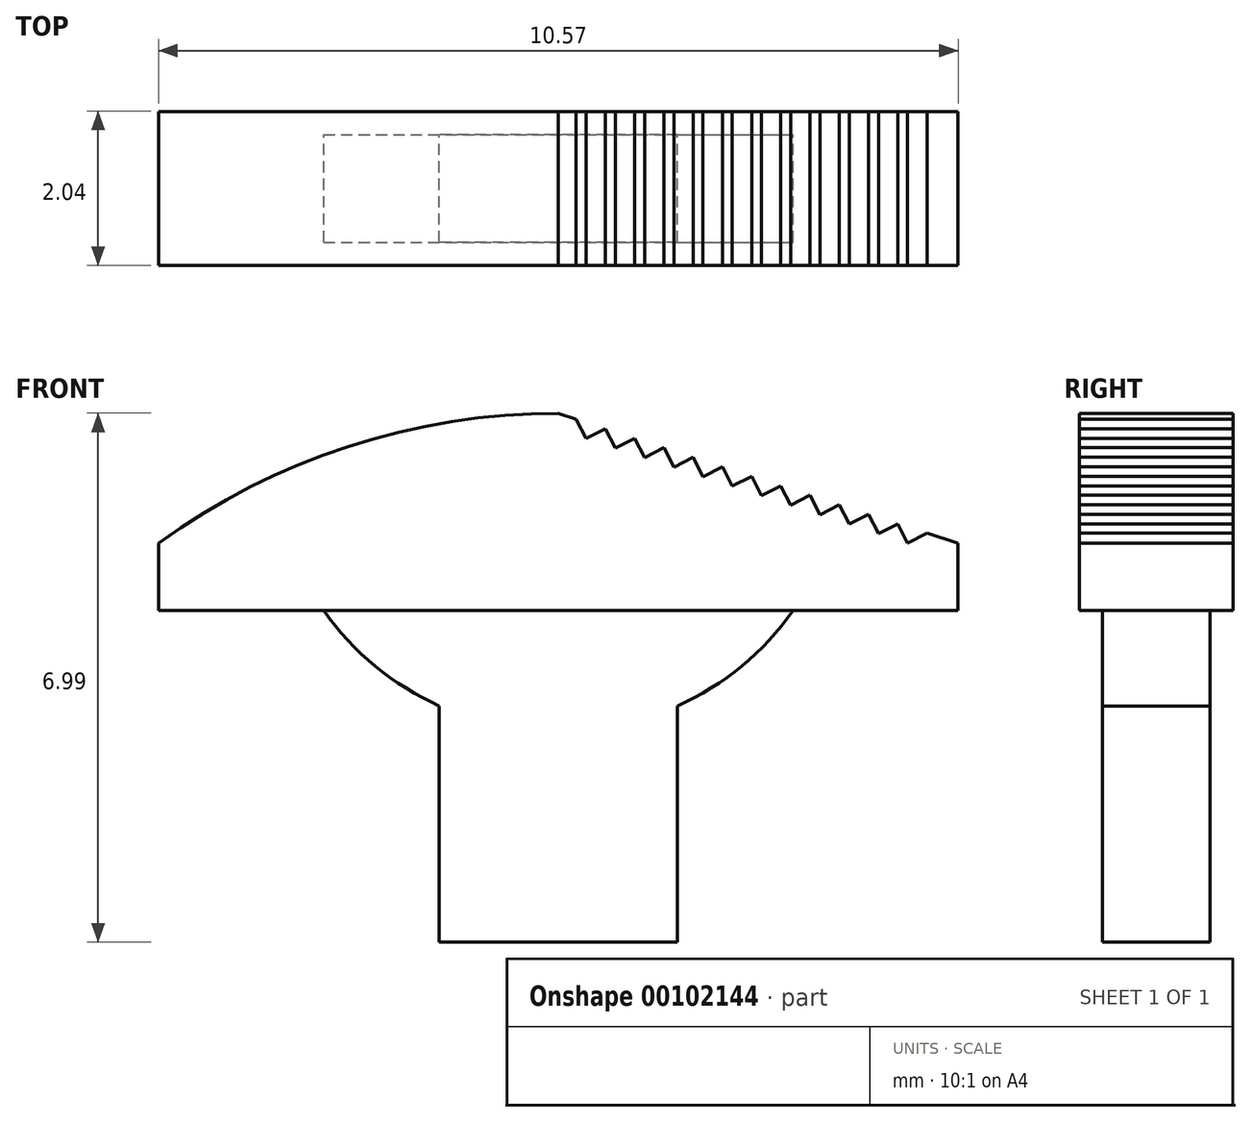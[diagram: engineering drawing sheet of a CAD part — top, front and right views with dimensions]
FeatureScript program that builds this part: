
annotation { "Feature Type Name" : "Feature", "Feature Type Description" : "" }
export const myFeature = defineFeature(function(context is Context, id is Id, definition is map)
    precondition{}
    {
        {
            var Q0;
            Q0=qCreatedBy(makeId("Front.planeOp"),FACE);
            var sketch = newSketch(context, id + "F0", { "sketchPlane" : qUnion([Q0])});
            skLineSegment(sketch, "E0", {"start": v(0, 0) * mm, "end": v(-3.15, 0) * mm});
            skLineSegment(sketch, "E1", {"start": v(-3.15, 0) * mm, "end": v(-3.15, 3.12) * mm});
            skLineSegment(sketch, "E2", {"start": v(3.7, 4.38) * mm, "end": v(1.53, 4.38) * mm});
            skLineSegment(sketch, "E3", {"start": v(-6.86, 4.38) * mm, "end": v(-6.86, 5.27) * mm});
            skLineSegment(sketch, "E4", {"start": v(3.7, 5.27) * mm, "end": v(3.7, 4.38) * mm});
            skArc(sketch, "E5", {"start": v(-4.68, 4.38) * mm, "mid": v(-4, 3.65) * mm, "end": v(-3.15, 3.12) * mm});
            skLineSegment(sketch, "E6", {"start": v(0, 0) * mm, "end": v(0, 3.12) * mm});
            skPoint(sketch, "E7", {"position": v(-1.57, 0) * mm});
            skLineSegment(sketch, "E8.trimOffspring", {"start": v(-4.68, 4.38) * mm, "end": v(-6.86, 4.38) * mm});
            skArc(sketch, "E9.trimOffspring", {"start": v(0, 3.12) * mm, "mid": v(0.85, 3.65) * mm, "end": v(1.53, 4.38) * mm});
            skArc(sketch, "E10", {"start": v(-1.57, 6.99) * mm, "mid": v(-4.35, 6.55) * mm, "end": v(-6.86, 5.27) * mm});
            skLineSegment(sketch, "E11", {"start": v(-1.57, 6.99) * mm, "end": v(3.7, 5.27) * mm});
            skLineSegment(sketch, "E12", {"start": v(-4.68, 4.38) * mm, "end": v(1.53, 4.38) * mm});
            skSolve(sketch);
        }
        {
            var Q0;
            Q0=makeQuery(id+"F0.imprint","IMPRINT",FACE,{"disambiguationData":[TD([[makeQuery(id+"F0.imprint","IMPRINT",EDGE,{"derivedFrom":sQuery(id+"F0.wireOp",EDGE,"E2")}),-1.0]])]});
            extrude(context, id + "F1", {"entities" : qUnion([Q0]), "depth" : 1.02 * mm, "hasSecondDirection" : true, "secondDirectionOppositeDirection" : true, "secondDirectionDepth" : 1.02 * mm});
        }
        {
            var Q0;
            Q0=makeQuery(id+"F0.imprint","IMPRINT",FACE,{"disambiguationData":[TD([[makeQuery(id+"F0.imprint","IMPRINT",EDGE,{"derivedFrom":sQuery(id+"F0.wireOp",EDGE,"E0")}),-1.0]])]});
            extrude(context, id + "F2", {"entities" : qUnion([Q0]), "operationType" : NewBodyOperationType.ADD, "depth" : 0.71 * mm, "hasSecondDirection" : true, "secondDirectionOppositeDirection" : true, "secondDirectionDepth" : 0.71 * mm});
        }
        {
            var Q0;
            Q0=makeQuery(id+"F1.opExtrude","CAP_FACE",FACE,{"disambiguationData":[OSD([sQuery(id+"F0.wireOp",EDGE,"E2"),sQuery(id+"F0.wireOp",EDGE,"E3"),sQuery(id+"F0.wireOp",EDGE,"E4"),sQuery(id+"F0.wireOp",EDGE,"E8.trimOffspring"),sQuery(id+"F0.wireOp",EDGE,"E10"),sQuery(id+"F0.wireOp",EDGE,"E11"),sQuery(id+"F0.wireOp",EDGE,"E12")])],"isStart":false});
            var sketch = newSketch(context, id + "F3", { "sketchPlane" : qUnion([Q0])});
            skLineSegment(sketch, "E13", {"start": v(3.3, 5.4) * mm, "end": v(3.04, 5.27) * mm});
            skLineSegment(sketch, "E14", {"start": v(3.04, 5.27) * mm, "end": v(2.91, 5.53) * mm});
            skLineSegment(sketch, "E15", {"start": v(2.91, 5.53) * mm, "end": v(2.66, 5.4) * mm});
            skLineSegment(sketch, "E16", {"start": v(2.66, 5.4) * mm, "end": v(2.52, 5.65) * mm});
            skLineSegment(sketch, "E17", {"start": v(2.52, 5.65) * mm, "end": v(2.27, 5.52) * mm});
            skLineSegment(sketch, "E18", {"start": v(2.27, 5.52) * mm, "end": v(2.14, 5.78) * mm});
            skLineSegment(sketch, "E19", {"start": v(2.14, 5.78) * mm, "end": v(1.88, 5.65) * mm});
            skLineSegment(sketch, "E20", {"start": v(1.88, 5.65) * mm, "end": v(1.75, 5.9) * mm});
            skLineSegment(sketch, "E21", {"start": v(1.75, 5.9) * mm, "end": v(1.5, 5.77) * mm});
            skLineSegment(sketch, "E22", {"start": v(1.5, 5.77) * mm, "end": v(1.37, 6.03) * mm});
            skLineSegment(sketch, "E23", {"start": v(1.37, 6.03) * mm, "end": v(1.1, 5.9) * mm});
            skLineSegment(sketch, "E24", {"start": v(1.1, 5.9) * mm, "end": v(0.98, 6.16) * mm});
            skLineSegment(sketch, "E25", {"start": v(0.98, 6.16) * mm, "end": v(0.72, 6.02) * mm});
            skLineSegment(sketch, "E26", {"start": v(0.72, 6.02) * mm, "end": v(0.6, 6.28) * mm});
            skLineSegment(sketch, "E27", {"start": v(0.6, 6.28) * mm, "end": v(0.34, 6.15) * mm});
            skLineSegment(sketch, "E28", {"start": v(0.34, 6.15) * mm, "end": v(0.2, 6.4) * mm});
            skLineSegment(sketch, "E29", {"start": v(0.2, 6.4) * mm, "end": v(-0.05, 6.28) * mm});
            skLineSegment(sketch, "E30", {"start": v(-0.05, 6.28) * mm, "end": v(-0.18, 6.53) * mm});
            skLineSegment(sketch, "E31", {"start": v(-0.18, 6.53) * mm, "end": v(-0.44, 6.4) * mm});
            skLineSegment(sketch, "E32", {"start": v(-0.44, 6.4) * mm, "end": v(-0.57, 6.66) * mm});
            skLineSegment(sketch, "E33", {"start": v(-0.57, 6.66) * mm, "end": v(-0.82, 6.53) * mm});
            skLineSegment(sketch, "E34", {"start": v(-0.82, 6.53) * mm, "end": v(-0.95, 6.78) * mm});
            skLineSegment(sketch, "E35", {"start": v(-0.95, 6.78) * mm, "end": v(-1.2, 6.65) * mm});
            skLineSegment(sketch, "E36", {"start": v(-1.2, 6.65) * mm, "end": v(-1.34, 6.9) * mm});
            skLineSegment(sketch, "E37", {"start": v(-1.34, 6.9) * mm, "end": v(3.3, 5.4) * mm});
            skSolve(sketch);
        }
        {
            var Q0;
            Q0 = qSketchRegion(id + "F3", true);
            extrude(context, id + "F4", {"entities" : qUnion([Q0]), "operationType" : NewBodyOperationType.REMOVE, "oppositeDirection" : true, "depth" : 25.4 * mm});
        }
    });
